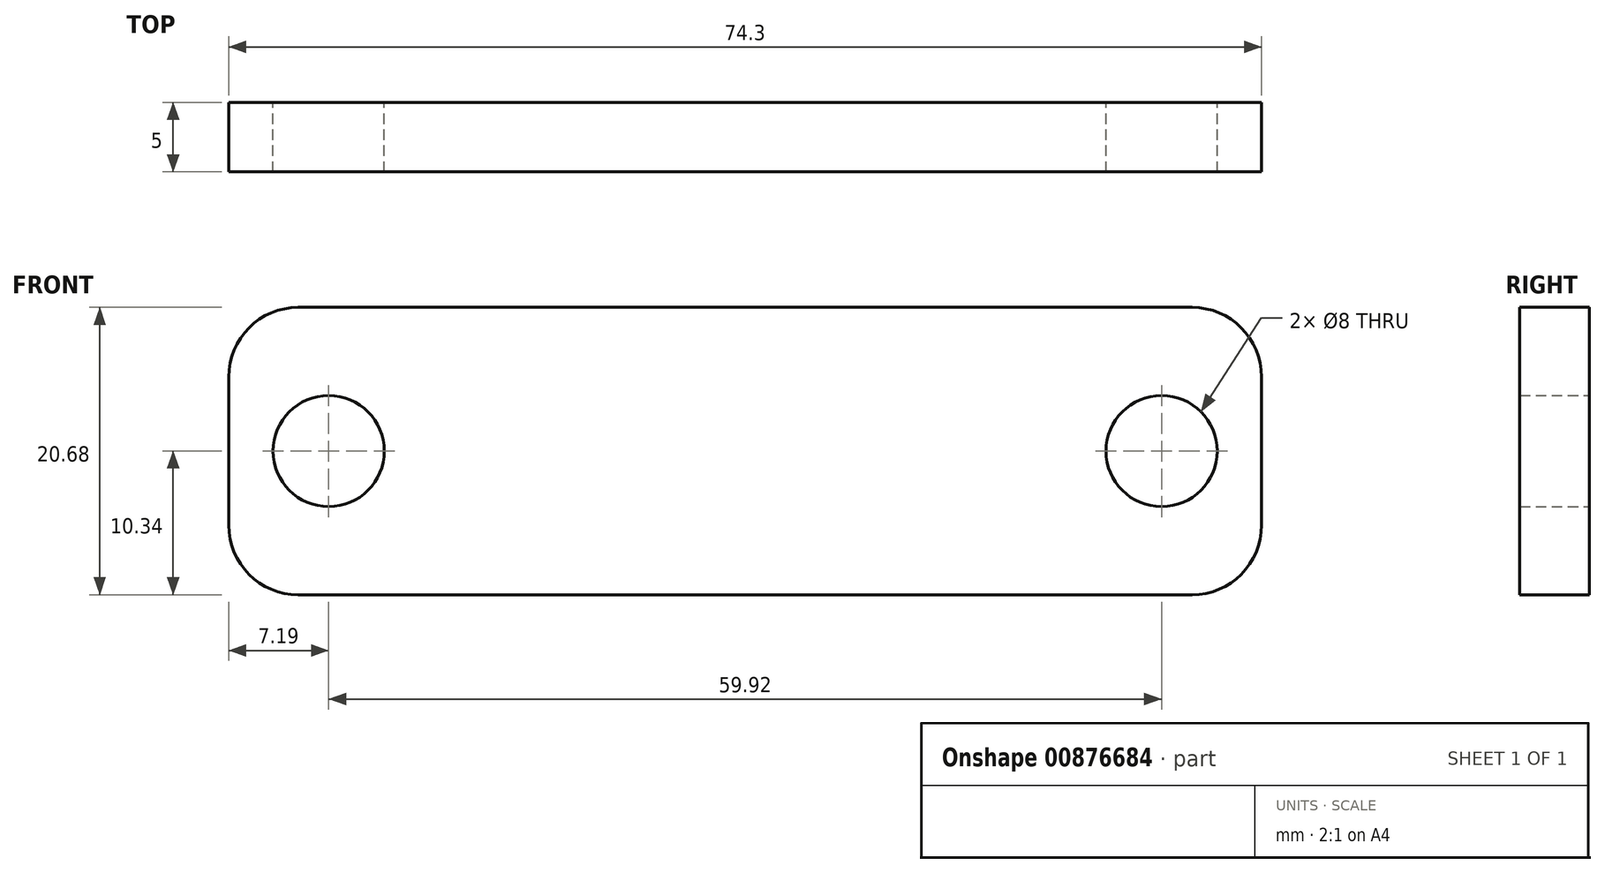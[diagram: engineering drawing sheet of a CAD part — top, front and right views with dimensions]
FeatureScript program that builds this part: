
annotation { "Feature Type Name" : "Feature", "Feature Type Description" : "" }
export const myFeature = defineFeature(function(context is Context, id is Id, definition is map)
    precondition{}
    {
        {
            var Q0;
            Q0=qCreatedBy(makeId("Front.planeOp"),FACE);
            var sketch = newSketch(context, id + "F0", { "sketchPlane" : qUnion([Q0])});
            skCircle(sketch, "E0", {"center": v(29.96, 0) * mm, "radius": 4 * mm});
            skCircle(sketch, "E1", {"center": v(-29.96, 0) * mm, "radius": 4 * mm});
            skLineSegment(sketch, "E2.bottom", {"start": v(37.15, -10.34) * mm, "end": v(-37.15, -10.34) * mm});
            skLineSegment(sketch, "E2.top", {"start": v(37.15, 10.34) * mm, "end": v(-37.15, 10.34) * mm});
            skLineSegment(sketch, "E2.left", {"start": v(37.15, -10.34) * mm, "end": v(37.15, 10.34) * mm});
            skLineSegment(sketch, "E2.right", {"start": v(-37.15, -10.34) * mm, "end": v(-37.15, 10.34) * mm});
            skPoint(sketch, "E2.middle", {"position": v(0, 0) * mm});
            skSolve(sketch);
        }
        {
            var Q0;
            Q0 = qSketchRegion(id + "F0", true);
            extrude(context, id + "F1", {"entities" : qUnion([Q0]), "depth" : 5 * mm, "offsetDistance" : 25 * mm});
        }
        {
            var Q0;
            Q0=makeQuery(id+"F1.opExtrude","SWEPT_EDGE",EDGE,{"disambiguationData":[OSD([sQuery(id+"F0.wireOp",EDGE,"E2.top"),sQuery(id+"F0.wireOp",EDGE,"E2.left")])]});
            var Q1;
            Q1=makeQuery(id+"F1.opExtrude","SWEPT_EDGE",EDGE,{"disambiguationData":[OSD([sQuery(id+"F0.wireOp",EDGE,"E2.bottom"),sQuery(id+"F0.wireOp",EDGE,"E2.left")])]});
            var Q2;
            Q2=makeQuery(id+"F1.opExtrude","SWEPT_EDGE",EDGE,{"disambiguationData":[OSD([sQuery(id+"F0.wireOp",EDGE,"E2.top"),sQuery(id+"F0.wireOp",EDGE,"E2.right")])]});
            var Q3;
            Q3=makeQuery(id+"F1.opExtrude","SWEPT_EDGE",EDGE,{"disambiguationData":[OSD([sQuery(id+"F0.wireOp",EDGE,"E2.bottom"),sQuery(id+"F0.wireOp",EDGE,"E2.right")])]});
            fillet(context, id + "F2", {"entities" : qUnion([Q0, Q1, Q2, Q3]), "radius" : 5 * mm, "tangentPropagation" : true, "allowEdgeOverflow" : false});
        }
    });
